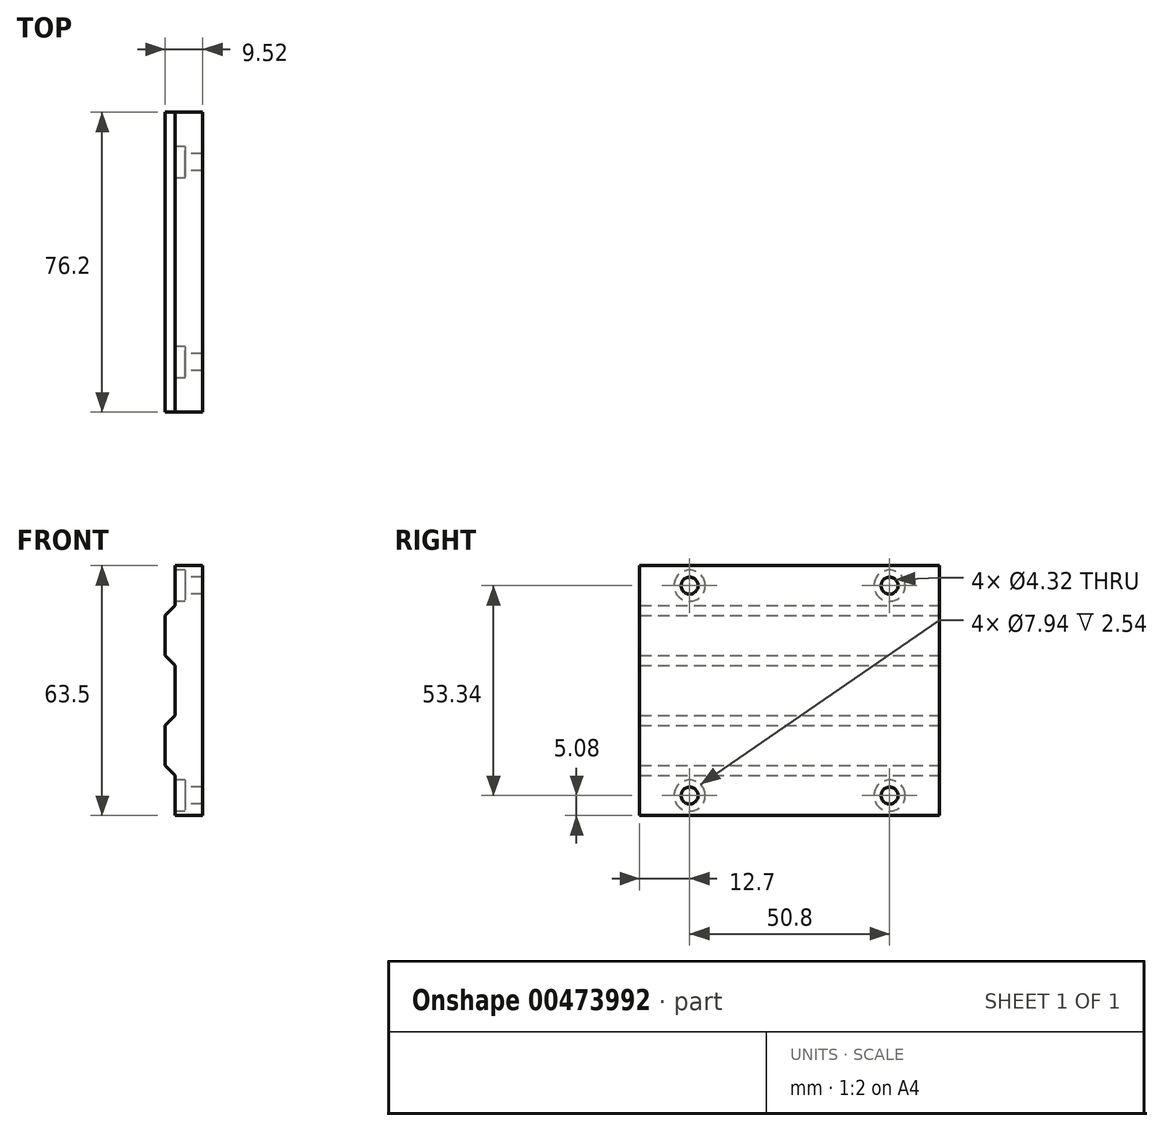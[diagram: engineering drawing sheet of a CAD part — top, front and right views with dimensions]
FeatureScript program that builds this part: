
annotation { "Feature Type Name" : "Feature", "Feature Type Description" : "" }
export const myFeature = defineFeature(function(context is Context, id is Id, definition is map)
    precondition{}
    {
        {
            var Q0;
            Q0=qCreatedBy(makeId("Front.planeOp"),FACE);
            var sketch = newSketch(context, id + "F0", { "sketchPlane" : qUnion([Q0])});
            skLineSegment(sketch, "E0.0.0", {"start": v(6.99, 40.64) * mm, "end": v(6.98, 50.8) * mm});
            skLineSegment(sketch, "E0.0.1", {"start": v(6.98, 50.8) * mm, "end": v(9.52, 53.34) * mm});
            skLineSegment(sketch, "E0.0.2", {"start": v(9.52, 53.34) * mm, "end": v(9.52, 63.5) * mm});
            skLineSegment(sketch, "E0.0.3", {"start": v(9.52, 63.5) * mm, "end": v(0, 63.5) * mm});
            skLineSegment(sketch, "E0.0.4", {"start": v(0, 63.5) * mm, "end": v(0, 0) * mm});
            skLineSegment(sketch, "E0.0.5", {"start": v(0, 0) * mm, "end": v(9.53, 0) * mm});
            skLineSegment(sketch, "E0.0.6", {"start": v(9.53, 0) * mm, "end": v(9.53, 10.16) * mm});
            skLineSegment(sketch, "E0.0.7", {"start": v(9.53, 10.16) * mm, "end": v(6.98, 12.7) * mm});
            skLineSegment(sketch, "E0.0.8", {"start": v(6.99, 12.7) * mm, "end": v(6.98, 22.86) * mm});
            skLineSegment(sketch, "E0.0.9", {"start": v(6.98, 22.86) * mm, "end": v(9.52, 25.4) * mm});
            skLineSegment(sketch, "E0.0.10", {"start": v(9.53, 25.4) * mm, "end": v(9.52, 38.1) * mm});
            skLineSegment(sketch, "E0.0.11", {"start": v(9.52, 38.1) * mm, "end": v(6.98, 40.64) * mm});
            skLineSegment(sketch, "E1", {"start": v(9.52, 63.5) * mm, "end": v(16.5, 63.5) * mm});
            skLineSegment(sketch, "E2", {"start": v(16.5, 63.5) * mm, "end": v(16.51, 0) * mm});
            skLineSegment(sketch, "E3", {"start": v(16.51, 0) * mm, "end": v(9.53, 0) * mm});
            skSolve(sketch);
        }
        {
            var Q0;
            Q0=makeQuery(id+"F0.imprint","IMPRINT",FACE,{"disambiguationData":[TD([[makeQuery(id+"F0.imprint","IMPRINT",EDGE,{"derivedFrom":sQuery(id+"F0.wireOp",EDGE,"E0.0.0")}),-1.0]])]});
            extrude(context, id + "F1", {"entities" : qUnion([Q0]), "depth" : 76.2 * mm});
        }
        {
            var Q0;
            Q0=makeQuery(id+"F1.opExtrude","SWEPT_FACE",FACE,{"disambiguationData":[OSD([sQuery(id+"F0.wireOp",EDGE,"E0.0.2")])]});
            var sketch = newSketch(context, id + "F2", { "sketchPlane" : qUnion([Q0])});
            skPoint(sketch, "E4", {"position": v(12.7, 58.42) * mm});
            skPoint(sketch, "E5", {"position": v(63.5, 58.42) * mm});
            skPoint(sketch, "E6", {"position": v(12.7, 5.08) * mm});
            skPoint(sketch, "E7", {"position": v(63.5, 5.08) * mm});
            skSolve(sketch);
        }
        {
            var Q0;
            Q0=sQuery(id+"F2.wireOp",VERTEX,"E4");
            var Q1;
            Q1=sQuery(id+"F2.wireOp",VERTEX,"E5");
            var Q2;
            Q2=sQuery(id+"F2.wireOp",VERTEX,"E6");
            var Q3;
            Q3=sQuery(id+"F2.wireOp",VERTEX,"E7");
            var Q4;
            Q4=makeQuery(id+"F1.opExtrude","SWEPT_BODY",BODY,{"disambiguationData":[OSD([sQuery(id+"F0.wireOp",EDGE,"E0.0.0"),sQuery(id+"F0.wireOp",EDGE,"E0.0.1"),sQuery(id+"F0.wireOp",EDGE,"E0.0.2"),sQuery(id+"F0.wireOp",EDGE,"E0.0.6"),sQuery(id+"F0.wireOp",EDGE,"E0.0.7"),sQuery(id+"F0.wireOp",EDGE,"E0.0.8"),sQuery(id+"F0.wireOp",EDGE,"E0.0.9"),sQuery(id+"F0.wireOp",EDGE,"E0.0.10"),sQuery(id+"F0.wireOp",EDGE,"E0.0.11"),sQuery(id+"F0.wireOp",EDGE,"E1"),sQuery(id+"F0.wireOp",EDGE,"E2"),sQuery(id+"F0.wireOp",EDGE,"E3")])]});
            hole(context, id + "F3", {"style" : HoleStyle.SIMPLE, "endStyle" : HoleEndStyle.BLIND, "standardTappedOrClearance" : lookupTablePath({ "standard" : "ANSI", "fit" : "Close", "size" : "#8", "type" : "Clearance" }), "standardBlindInLast" : lookupTablePath({ "fit" : "Close", "standard" : "ANSI", "size" : "#8", "type" : "Clearance" }), "holeDiameter" : 4.32 * mm, "holeDepth" : 12.7 * mm, "isTappedThrough" : true, "tappedDepth" : 10.32 * mm, "tapClearance" : 3, "locations" : qUnion([Q0, Q1, Q2, Q3]), "scope" : qUnion([Q4])});
        }
        {
            var Q0;
            Q0=makeQuery(id+"F1.opExtrude","SWEPT_FACE",FACE,{"disambiguationData":[OSD([sQuery(id+"F0.wireOp",EDGE,"E0.0.2")])]});
            var sketch = newSketch(context, id + "F4", { "sketchPlane" : qUnion([Q0])});
            skCircle(sketch, "E8.0", {"center": v(12.7, 5.08) * mm, "radius": 2.16 * mm});
            skCircle(sketch, "E9.0", {"center": v(63.5, 5.08) * mm, "radius": 2.16 * mm});
            skCircle(sketch, "E10", {"center": v(12.7, 58.42) * mm, "radius": 3.97 * mm});
            skCircle(sketch, "E11", {"center": v(63.5, 58.42) * mm, "radius": 3.97 * mm});
            skCircle(sketch, "E12", {"center": v(12.7, 5.08) * mm, "radius": 3.97 * mm});
            skCircle(sketch, "E13", {"center": v(63.5, 5.08) * mm, "radius": 3.97 * mm});
            skSolve(sketch);
        }
        {
            var Q0;
            Q0=makeQuery(id+"F4.imprint","IMPRINT",FACE,{"disambiguationData":[TD([[makeQuery(id+"F4.imprint","IMPRINT",EDGE,{"derivedFrom":sQuery(id+"F4.wireOp",EDGE,"E10")}),1.0]])]});
            var Q1;
            Q1=makeQuery(id+"F4.imprint","IMPRINT",FACE,{"disambiguationData":[TD([[makeQuery(id+"F4.imprint","IMPRINT",EDGE,{"derivedFrom":sQuery(id+"F4.wireOp",EDGE,"E11")}),1.0]])]});
            var Q2;
            Q2=makeQuery(id+"F4.imprint","IMPRINT",FACE,{"disambiguationData":[TD([[makeQuery(id+"F4.imprint","IMPRINT",EDGE,{"derivedFrom":sQuery(id+"F4.wireOp",EDGE,"E8.0")}),-1.0]])]});
            var Q3;
            Q3=makeQuery(id+"F4.imprint","IMPRINT",FACE,{"disambiguationData":[TD([[makeQuery(id+"F4.imprint","IMPRINT",EDGE,{"derivedFrom":sQuery(id+"F4.wireOp",EDGE,"E9.0")}),-1.0]])]});
            extrude(context, id + "F5", {"entities" : qUnion([Q0, Q1, Q2, Q3]), "operationType" : NewBodyOperationType.REMOVE, "oppositeDirection" : true, "depth" : 2.54 * mm, "offsetDistance" : 25.4 * mm});
        }
    });
